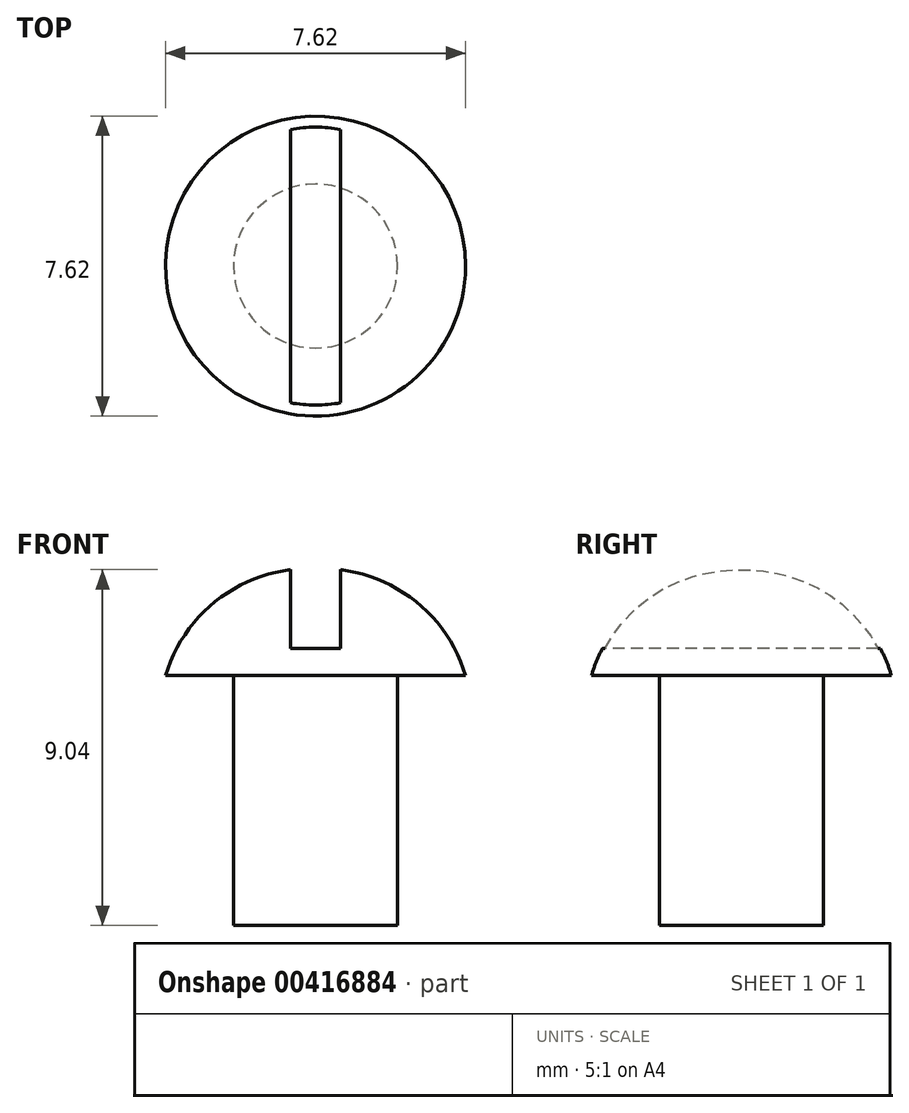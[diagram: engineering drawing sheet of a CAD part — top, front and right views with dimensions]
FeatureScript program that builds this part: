
annotation { "Feature Type Name" : "Feature", "Feature Type Description" : "" }
export const myFeature = defineFeature(function(context is Context, id is Id, definition is map)
    precondition{}
    {
        {
            var Q0;
            Q0=qCreatedBy(makeId("Top.planeOp"),FACE);
            var sketch = newSketch(context, id + "F0", { "sketchPlane" : qUnion([Q0])});
            skCircle(sketch, "E0", {"center": v(0, 0) * mm, "radius": 2.08 * mm});
            skCircle(sketch, "E1", {"center": v(0, 0) * mm, "radius": 3.81 * mm});
            skSolve(sketch);
        }
        {
            var Q0;
            Q0=makeQuery(id+"F0.imprint","IMPRINT",FACE,{"disambiguationData":[TD([[makeQuery(id+"F0.imprint","IMPRINT",EDGE,{"derivedFrom":sQuery(id+"F0.wireOp",EDGE,"E0")}),1.0]])]});
            extrude(context, id + "F1", {"entities" : qUnion([Q0]), "oppositeDirection" : true, "depth" : 6.35 * mm});
        }
        {
            var Q0;
            Q0=makeQuery(id+"F0.imprint","IMPRINT",FACE,{"disambiguationData":[TD([[makeQuery(id+"F0.imprint","IMPRINT",EDGE,{"derivedFrom":sQuery(id+"F0.wireOp",EDGE,"E0")}),1.0]])]});
            var Q1;
            Q1=makeQuery(id+"F0.imprint","IMPRINT",FACE,{"disambiguationData":[TD([[makeQuery(id+"F0.imprint","IMPRINT",EDGE,{"derivedFrom":sQuery(id+"F0.wireOp",EDGE,"E0")}),-1.0]])]});
            extrude(context, id + "F2", {"entities" : qUnion([Q0, Q1]), "operationType" : NewBodyOperationType.ADD, "depth" : 2.72 * mm});
        }
        {
            var Q0;
            Q0=makeQuery(id+"F2.opExtrude","CAP_EDGE",EDGE,{"disambiguationData":[OSD([sQuery(id+"F0.wireOp",EDGE,"E1")])],"isStart":false});
            fillet(context, id + "F3", {"entities" : qUnion([Q0]), "radius" : 3.8 * mm, "tangentPropagation" : true, "allowEdgeOverflow" : false});
        }
        {
            var Q0;
            Q0=qCreatedBy(makeId("Front.planeOp"),FACE);
            var sketch = newSketch(context, id + "F4", { "sketchPlane" : qUnion([Q0])});
            skLineSegment(sketch, "E2", {"start": v(0, 0) * mm, "end": v(0, 5.03) * mm, "construction": true});
            skLineSegment(sketch, "E3.0", {"start": v(-0.16, 2.72) * mm, "end": v(0.16, 2.72) * mm});
            skLineSegment(sketch, "E4.bottom", {"start": v(0.63, 0.69) * mm, "end": v(-0.64, 0.69) * mm});
            skLineSegment(sketch, "E4.top", {"start": v(0.64, 4.75) * mm, "end": v(-0.64, 4.75) * mm});
            skLineSegment(sketch, "E4.left", {"start": v(0.63, 0.69) * mm, "end": v(0.64, 4.75) * mm});
            skLineSegment(sketch, "E4.right", {"start": v(-0.64, 0.69) * mm, "end": v(-0.64, 4.75) * mm});
            skPoint(sketch, "E4.middle", {"position": v(0, 2.72) * mm});
            skSolve(sketch);
        }
        {
            var Q0;
            Q0=makeQuery(id+"F4.imprint","IMPRINT",FACE,{"disambiguationData":[TD([[makeQuery(id+"F4.imprint","IMPRINT",EDGE,{"derivedFrom":sQuery(id+"F4.wireOp",EDGE,"E4.bottom")}),-1.0]])]});
            extrude(context, id + "F5", {"entities" : qUnion([Q0]), "operationType" : NewBodyOperationType.REMOVE, "endBound" : BoundingType.SYMMETRIC, "oppositeDirection" : true, "depth" : 7.62 * mm});
        }
    });
